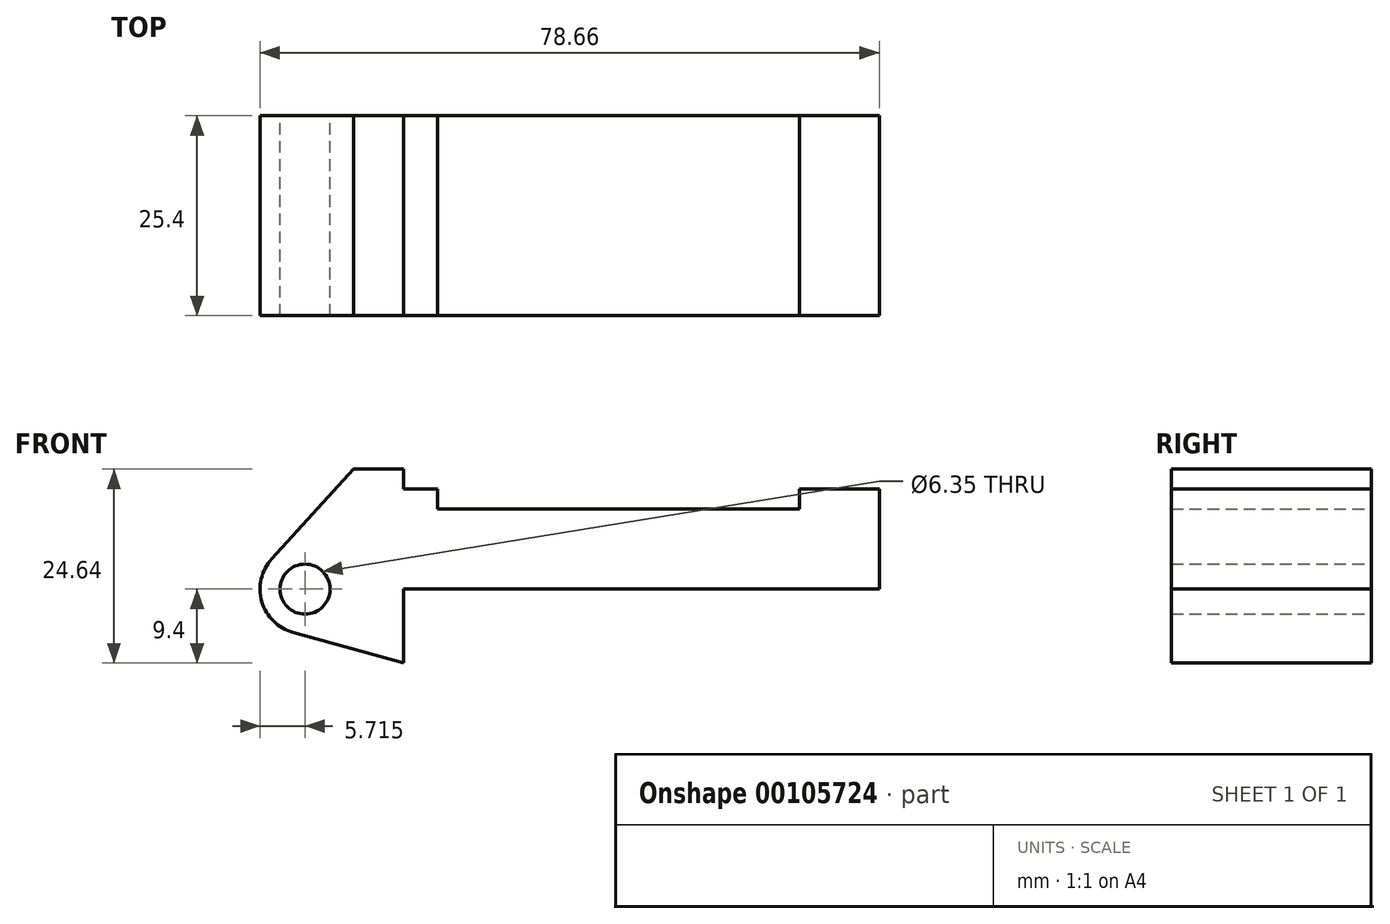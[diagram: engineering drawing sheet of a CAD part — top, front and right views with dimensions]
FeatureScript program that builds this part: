
annotation { "Feature Type Name" : "Feature", "Feature Type Description" : "" }
export const myFeature = defineFeature(function(context is Context, id is Id, definition is map)
    precondition{}
    {
        {
            var Q0;
            Q0=qCreatedBy(makeId("Front.planeOp"),FACE);
            var sketch = newSketch(context, id + "F0", { "sketchPlane" : qUnion([Q0])});
            skLineSegment(sketch, "E0", {"start": v(0, 0) * mm, "end": v(0, 12.7) * mm});
            skLineSegment(sketch, "E1", {"start": v(0, 12.7) * mm, "end": v(10.16, 12.7) * mm});
            skLineSegment(sketch, "E2", {"start": v(10.16, 12.7) * mm, "end": v(10.16, 10.16) * mm});
            skLineSegment(sketch, "E3", {"start": v(10.16, 10.16) * mm, "end": v(56.13, 10.16) * mm});
            skLineSegment(sketch, "E4", {"start": v(56.13, 10.16) * mm, "end": v(56.13, 12.7) * mm});
            skLineSegment(sketch, "E5", {"start": v(56.13, 12.7) * mm, "end": v(66.3, 12.7) * mm});
            skLineSegment(sketch, "E6", {"start": v(66.3, 12.7) * mm, "end": v(66.3, 0) * mm});
            skLineSegment(sketch, "E7", {"start": v(66.3, 0) * mm, "end": v(0, 0) * mm});
            skLineSegment(sketch, "E8", {"start": v(5.84, 15.24) * mm, "end": v(-0.5, 15.24) * mm});
            skLineSegment(sketch, "E9", {"start": v(-0.5, 15.24) * mm, "end": v(-10.88, 3.85) * mm});
            skLineSegment(sketch, "E10", {"start": v(0, 0) * mm, "end": v(-6.65, 0) * mm});
            skCircle(sketch, "E11", {"center": v(-6.65, 0) * mm, "radius": 5.72 * mm});
            skCircle(sketch, "E12", {"center": v(-6.65, 0) * mm, "radius": 3.18 * mm});
            skLineSegment(sketch, "E13", {"start": v(5.84, 15.24) * mm, "end": v(5.84, -9.4) * mm});
            skLineSegment(sketch, "E14", {"start": v(5.84, -9.4) * mm, "end": v(-8.18, -5.5) * mm});
            skSolve(sketch);
        }
        {
            var Q0;
            {var subQ0=sQuery(id+"F0.wireOp",EDGE,"E2");Q0=makeQuery(id+"F0.imprint","IMPRINT",FACE,{"disambiguationData":[TD([[makeQuery(id+"F0.imprint","IMPRINT",EDGE,{"derivedFrom":subQ0}),-1.0]])]});}
            var Q1;
            {var subQ0=sQuery(id+"F0.wireOp",EDGE,"E0");Q1=makeQuery(id+"F0.imprint","IMPRINT",FACE,{"disambiguationData":[TD([[makeQuery(id+"F0.imprint","IMPRINT",EDGE,{"derivedFrom":subQ0}),-1.0]])]});}
            var Q2;
            {var subQ3=sQuery(id+"F0.wireOp",EDGE,"E0");Q2=makeQuery(id+"F0.imprint","IMPRINT",FACE,{"disambiguationData":[TD([[makeQuery(id+"F0.imprint","IMPRINT",EDGE,{"derivedFrom":subQ3}),1.0]])]});}
            var Q3;
            {var subQ0=sQuery(id+"F0.wireOp",EDGE,"E14");Q3=makeQuery(id+"F0.imprint","IMPRINT",FACE,{"disambiguationData":[TD([[makeQuery(id+"F0.imprint","IMPRINT",EDGE,{"derivedFrom":subQ0}),-1.0]])]});}
            var Q4;
            {var subQ4=sQuery(id+"F0.wireOp",EDGE,"E12");Q4=makeQuery(id+"F0.imprint","IMPRINT",FACE,{"disambiguationData":[TD([[makeQuery(id+"F0.imprint","IMPRINT",EDGE,{"derivedFrom":subQ4}),-1.0]])]});}
            extrude(context, id + "F1", {"entities" : qUnion([Q0, Q1, Q2, Q3, Q4]), "depth" : 25.4 * mm});
        }
    });
